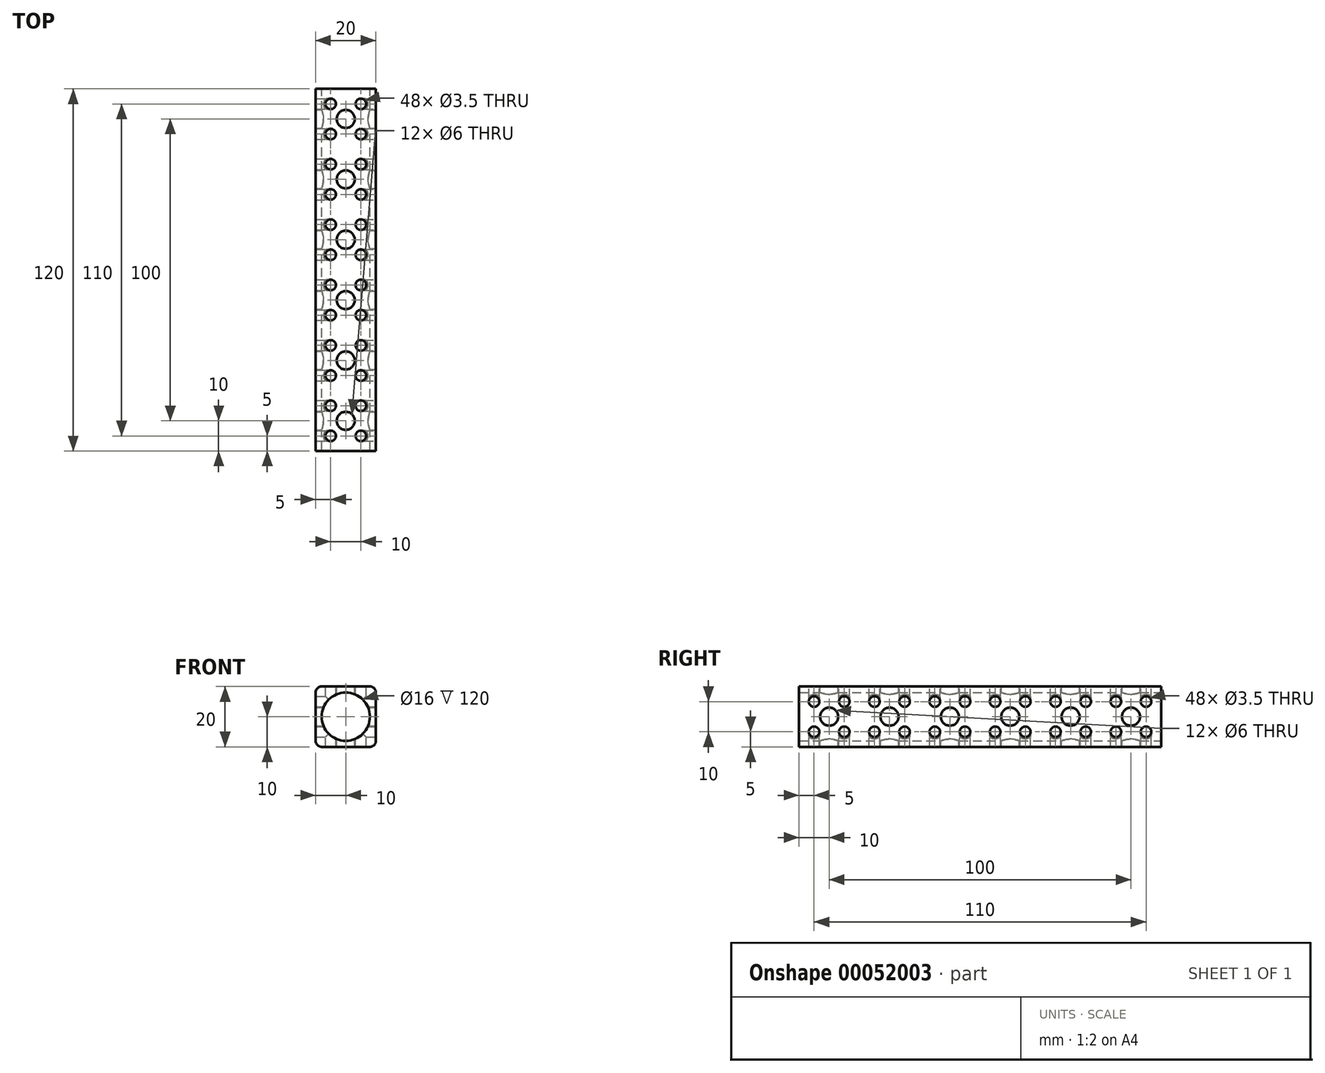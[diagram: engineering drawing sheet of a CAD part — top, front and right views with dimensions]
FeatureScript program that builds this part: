
annotation { "Feature Type Name" : "Feature", "Feature Type Description" : "" }
export const myFeature = defineFeature(function(context is Context, id is Id, definition is map)
    precondition{}
    {
        {
            var Q0;
            Q0=qCreatedBy(makeId("Front.planeOp"),FACE);
            var sketch = newSketch(context, id + "F0", { "sketchPlane" : qUnion([Q0])});
            skLineSegment(sketch, "E0.bottom", {"start": v(-10, 10) * mm, "end": v(10, 10) * mm});
            skLineSegment(sketch, "E0.top", {"start": v(-10, -10) * mm, "end": v(10, -10) * mm});
            skLineSegment(sketch, "E0.left", {"start": v(-10, 10) * mm, "end": v(-10, -10) * mm});
            skLineSegment(sketch, "E0.right", {"start": v(10, 10) * mm, "end": v(10, -10) * mm});
            skCircle(sketch, "E1", {"center": v(0, 0) * mm, "radius": 8 * mm});
            skLineSegment(sketch, "E2", {"start": v(-10, 10) * mm, "end": v(10, -10) * mm, "construction": true});
            skSolve(sketch);
        }
        {
            var Q0;
            Q0=makeQuery(id+"F0.imprint","IMPRINT",FACE,{"disambiguationData":[TD([[makeQuery(id+"F0.imprint","IMPRINT",EDGE,{"derivedFrom":sQuery(id+"F0.wireOp",EDGE,"E0.bottom")}),-1.0]])]});
            extrude(context, id + "F1", {"entities" : qUnion([Q0]), "endBound" : BoundingType.SYMMETRIC, "depth" : 120 * mm});
        }
        {
            var Q0;
            Q0=makeQuery(id+"F1.opExtrude","SWEPT_FACE",FACE,{"disambiguationData":[OSD([sQuery(id+"F0.wireOp",EDGE,"E0.right")])]});
            var sketch = newSketch(context, id + "F2", { "sketchPlane" : qUnion([Q0])});
            skLineSegment(sketch, "E3.bottom", {"start": v(-5, 5) * mm, "end": v(5, 5) * mm});
            skLineSegment(sketch, "E3.top", {"start": v(-5, -5) * mm, "end": v(5, -5) * mm});
            skLineSegment(sketch, "E3.left", {"start": v(-5, 5) * mm, "end": v(-5, -5) * mm});
            skLineSegment(sketch, "E3.right", {"start": v(5, 5) * mm, "end": v(5, -5) * mm});
            skLineSegment(sketch, "E4", {"start": v(-5, 5) * mm, "end": v(5, -5) * mm, "construction": true});
            skPoint(sketch, "E5", {"position": v(0, 0) * mm});
            skLineSegment(sketch, "E6.1.0.0", {"start": v(15, 5) * mm, "end": v(15, -5) * mm});
            skLineSegment(sketch, "E6.2.0.0", {"start": v(25, 5) * mm, "end": v(25, -5) * mm});
            skLineSegment(sketch, "E6.direction1", {"start": v(5, -5) * mm, "end": v(15, -5) * mm, "construction": true});
            skLineSegment(sketch, "E7.0.3.0", {"start": v(35, 5) * mm, "end": v(35, -5) * mm});
            skLineSegment(sketch, "E7.0.4.0", {"start": v(45, 5) * mm, "end": v(45, -5) * mm});
            skLineSegment(sketch, "E7.0.5.0", {"start": v(55, 5) * mm, "end": v(55, -5) * mm});
            skLineSegment(sketch, "E8.1.0.0", {"start": v(-15, 5) * mm, "end": v(-15, -5) * mm});
            skLineSegment(sketch, "E8.2.0.0", {"start": v(-25, 5) * mm, "end": v(-25, -5) * mm});
            skLineSegment(sketch, "E8.3.0.0", {"start": v(-35, 5) * mm, "end": v(-35, -5) * mm});
            skLineSegment(sketch, "E8.4.0.0", {"start": v(-45, 5) * mm, "end": v(-45, -5) * mm});
            skLineSegment(sketch, "E8.5.0.0", {"start": v(-55, 5) * mm, "end": v(-55, -5) * mm});
            skLineSegment(sketch, "E8.direction1", {"start": v(-5, -5) * mm, "end": v(-15, -5) * mm, "construction": true});
            skSolve(sketch);
        }
        {
            var Q0;
            Q0=sQuery(id+"F2.wireOp",VERTEX,"E8.5.0.0.start");
            var Q1;
            Q1=sQuery(id+"F2.wireOp",VERTEX,"E8.5.0.0.end");
            var Q2;
            Q2=sQuery(id+"F2.wireOp",VERTEX,"E8.4.0.0.end");
            var Q3;
            Q3=sQuery(id+"F2.wireOp",VERTEX,"E8.4.0.0.start");
            var Q4;
            Q4=sQuery(id+"F2.wireOp",VERTEX,"E8.3.0.0.start");
            var Q5;
            Q5=sQuery(id+"F2.wireOp",VERTEX,"E8.3.0.0.end");
            var Q6;
            Q6=sQuery(id+"F2.wireOp",VERTEX,"E8.2.0.0.end");
            var Q7;
            Q7=sQuery(id+"F2.wireOp",VERTEX,"E8.2.0.0.start");
            var Q8;
            Q8=sQuery(id+"F2.wireOp",VERTEX,"E8.direction1.end");
            var Q9;
            Q9=sQuery(id+"F2.wireOp",VERTEX,"E8.1.0.0.start");
            var Q10;
            Q10=sQuery(id+"F2.wireOp",VERTEX,"E3.left.end");
            var Q11;
            Q11=sQuery(id+"F2.wireOp",VERTEX,"E3.left.start");
            var Q12;
            Q12=sQuery(id+"F2.wireOp",VERTEX,"E3.top.end");
            var Q13;
            Q13=sQuery(id+"F2.wireOp",VERTEX,"E3.right.start");
            var Q14;
            Q14=sQuery(id+"F2.wireOp",VERTEX,"E6.direction1.end");
            var Q15;
            Q15=sQuery(id+"F2.wireOp",VERTEX,"E6.1.0.0.start");
            var Q16;
            Q16=sQuery(id+"F2.wireOp",VERTEX,"E6.2.0.0.end");
            var Q17;
            Q17=sQuery(id+"F2.wireOp",VERTEX,"E6.2.0.0.start");
            var Q18;
            Q18=sQuery(id+"F2.wireOp",VERTEX,"E7.0.3.0.start");
            var Q19;
            Q19=sQuery(id+"F2.wireOp",VERTEX,"E7.0.3.0.end");
            var Q20;
            Q20=sQuery(id+"F2.wireOp",VERTEX,"E7.0.4.0.end");
            var Q21;
            Q21=sQuery(id+"F2.wireOp",VERTEX,"E7.0.4.0.start");
            var Q22;
            Q22=sQuery(id+"F2.wireOp",VERTEX,"E7.0.5.0.end");
            var Q23;
            Q23=sQuery(id+"F2.wireOp",VERTEX,"E7.0.5.0.start");
            var Q24;
            Q24=makeQuery(id+"F1.opExtrude","SWEPT_BODY",BODY,{"disambiguationData":[OSD([sQuery(id+"F0.wireOp",EDGE,"E0.bottom"),sQuery(id+"F0.wireOp",EDGE,"E0.top"),sQuery(id+"F0.wireOp",EDGE,"E0.left"),sQuery(id+"F0.wireOp",EDGE,"E0.right"),sQuery(id+"F0.wireOp",EDGE,"E1")])]});
            hole(context, id + "F3", {"style" : HoleStyle.SIMPLE, "endStyle" : HoleEndStyle.THROUGH, "holeDiameter" : 3.5 * mm, "tappedDepth" : 12 * mm, "tapClearance" : 3, "locations" : qUnion([Q0, Q1, Q2, Q3, Q4, Q5, Q6, Q7, Q8, Q9, Q10, Q11, Q12, Q13, Q14, Q15, Q16, Q17, Q18, Q19, Q20, Q21, Q22, Q23]), "scope" : qUnion([Q24])});
        }
        {
            var Q0;
            Q0=makeQuery(id+"F1.opExtrude","SWEPT_FACE",FACE,{"disambiguationData":[OSD([sQuery(id+"F0.wireOp",EDGE,"E0.bottom")])]});
            var sketch = newSketch(context, id + "F4", { "sketchPlane" : qUnion([Q0])});
            skLineSegment(sketch, "E9.bottom", {"start": v(-5, 5) * mm, "end": v(5, 5) * mm});
            skLineSegment(sketch, "E9.top", {"start": v(-5, -5) * mm, "end": v(5, -5) * mm});
            skLineSegment(sketch, "E9.left", {"start": v(-5, 5) * mm, "end": v(-5, -5) * mm});
            skLineSegment(sketch, "E9.right", {"start": v(5, 5) * mm, "end": v(5, -5) * mm});
            skLineSegment(sketch, "E10", {"start": v(-5, 5) * mm, "end": v(5, -5) * mm, "construction": true});
            skPoint(sketch, "E11", {"position": v(0, 0) * mm});
            skLineSegment(sketch, "E12.0.1.0", {"start": v(-5, 15) * mm, "end": v(5, 15) * mm});
            skLineSegment(sketch, "E12.0.2.0", {"start": v(-5, 25) * mm, "end": v(5, 25) * mm});
            skLineSegment(sketch, "E12.0.3.0", {"start": v(-5, 35) * mm, "end": v(5, 35) * mm});
            skLineSegment(sketch, "E12.0.4.0", {"start": v(-5, 45) * mm, "end": v(5, 45) * mm});
            skLineSegment(sketch, "E12.0.5.0", {"start": v(-5, 55) * mm, "end": v(5, 55) * mm});
            skLineSegment(sketch, "E12.direction1", {"start": v(-5, 5) * mm, "end": v(20, 5) * mm, "construction": true});
            skLineSegment(sketch, "E12.direction2", {"start": v(-5, 5) * mm, "end": v(-5, 15) * mm, "construction": true});
            skLineSegment(sketch, "E13.0.1.0", {"start": v(-5, -15) * mm, "end": v(5, -15) * mm});
            skLineSegment(sketch, "E13.0.2.0", {"start": v(-5, -25) * mm, "end": v(5, -25) * mm});
            skLineSegment(sketch, "E13.0.3.0", {"start": v(-5, -35) * mm, "end": v(5, -35) * mm});
            skLineSegment(sketch, "E13.0.4.0", {"start": v(-5, -45) * mm, "end": v(5, -45) * mm});
            skLineSegment(sketch, "E13.0.5.0", {"start": v(-5, -55) * mm, "end": v(5, -55) * mm});
            skLineSegment(sketch, "E13.direction1", {"start": v(-5, -5) * mm, "end": v(5, -5) * mm, "construction": true});
            skLineSegment(sketch, "E13.direction2", {"start": v(-5, -5) * mm, "end": v(-5, -15) * mm, "construction": true});
            skSolve(sketch);
        }
        {
            var Q0;
            Q0=sQuery(id+"F4.wireOp",VERTEX,"E12.0.5.0.start");
            var Q1;
            Q1=sQuery(id+"F4.wireOp",VERTEX,"E12.0.5.0.end");
            var Q2;
            Q2=sQuery(id+"F4.wireOp",VERTEX,"E12.0.4.0.end");
            var Q3;
            Q3=sQuery(id+"F4.wireOp",VERTEX,"E12.0.4.0.start");
            var Q4;
            Q4=sQuery(id+"F4.wireOp",VERTEX,"E12.0.3.0.start");
            var Q5;
            Q5=sQuery(id+"F4.wireOp",VERTEX,"E12.0.3.0.end");
            var Q6;
            Q6=sQuery(id+"F4.wireOp",VERTEX,"E12.0.2.0.end");
            var Q7;
            Q7=sQuery(id+"F4.wireOp",VERTEX,"E12.0.2.0.start");
            var Q8;
            Q8=sQuery(id+"F4.wireOp",VERTEX,"E12.direction2.end");
            var Q9;
            Q9=sQuery(id+"F4.wireOp",VERTEX,"E12.0.1.0.end");
            var Q10;
            Q10=sQuery(id+"F4.wireOp",VERTEX,"E9.bottom.end");
            var Q11;
            Q11=sQuery(id+"F4.wireOp",VERTEX,"E12.direction1.start");
            var Q12;
            Q12=sQuery(id+"F4.wireOp",VERTEX,"E13.direction1.start");
            var Q13;
            Q13=sQuery(id+"F4.wireOp",VERTEX,"E9.top.end");
            var Q14;
            Q14=sQuery(id+"F4.wireOp",VERTEX,"E13.0.1.0.end");
            var Q15;
            Q15=sQuery(id+"F4.wireOp",VERTEX,"E13.direction2.end");
            var Q16;
            Q16=sQuery(id+"F4.wireOp",VERTEX,"E13.0.2.0.start");
            var Q17;
            Q17=sQuery(id+"F4.wireOp",VERTEX,"E13.0.2.0.end");
            var Q18;
            Q18=sQuery(id+"F4.wireOp",VERTEX,"E13.0.3.0.end");
            var Q19;
            Q19=sQuery(id+"F4.wireOp",VERTEX,"E13.0.3.0.start");
            var Q20;
            Q20=sQuery(id+"F4.wireOp",VERTEX,"E13.0.4.0.start");
            var Q21;
            Q21=sQuery(id+"F4.wireOp",VERTEX,"E13.0.4.0.end");
            var Q22;
            Q22=sQuery(id+"F4.wireOp",VERTEX,"E13.0.5.0.end");
            var Q23;
            Q23=sQuery(id+"F4.wireOp",VERTEX,"E13.0.5.0.start");
            var Q24;
            Q24=makeQuery(id+"F1.opExtrude","SWEPT_BODY",BODY,{"disambiguationData":[OSD([sQuery(id+"F0.wireOp",EDGE,"E0.bottom"),sQuery(id+"F0.wireOp",EDGE,"E0.top"),sQuery(id+"F0.wireOp",EDGE,"E0.left"),sQuery(id+"F0.wireOp",EDGE,"E0.right"),sQuery(id+"F0.wireOp",EDGE,"E1")])]});
            hole(context, id + "F5", {"style" : HoleStyle.SIMPLE, "endStyle" : HoleEndStyle.THROUGH, "holeDiameter" : 3.5 * mm, "tappedDepth" : 12 * mm, "tapClearance" : 3, "locations" : qUnion([Q0, Q1, Q2, Q3, Q4, Q5, Q6, Q7, Q8, Q9, Q10, Q11, Q12, Q13, Q14, Q15, Q16, Q17, Q18, Q19, Q20, Q21, Q22, Q23]), "scope" : qUnion([Q24])});
        }
        {
            var Q0;
            Q0=makeQuery(id+"F1.opExtrude","SWEPT_FACE",FACE,{"disambiguationData":[OSD([sQuery(id+"F0.wireOp",EDGE,"E0.right")])]});
            var sketch = newSketch(context, id + "F6", { "sketchPlane" : qUnion([Q0])});
            skPoint(sketch, "E14", {"position": v(0, 0) * mm});
            skPoint(sketch, "E15.1.0.0", {"position": v(10, 0) * mm});
            skPoint(sketch, "E15.2.0.0", {"position": v(20, 0) * mm});
            skPoint(sketch, "E15.3.0.0", {"position": v(30, 0) * mm});
            skPoint(sketch, "E15.4.0.0", {"position": v(40, 0) * mm});
            skPoint(sketch, "E15.5.0.0", {"position": v(50, 0) * mm});
            skLineSegment(sketch, "E15.direction1", {"start": v(0, 0) * mm, "end": v(10, 0) * mm, "construction": true});
            skPoint(sketch, "E16.1.0.0", {"position": v(-10, 0) * mm});
            skPoint(sketch, "E16.2.0.0", {"position": v(-20, 0) * mm});
            skPoint(sketch, "E16.3.0.0", {"position": v(-30, 0) * mm});
            skPoint(sketch, "E16.4.0.0", {"position": v(-40, 0) * mm});
            skPoint(sketch, "E16.5.0.0", {"position": v(-50, 0) * mm});
            skLineSegment(sketch, "E16.direction1", {"start": v(0, 0) * mm, "end": v(-10, 0) * mm, "construction": true});
            skSolve(sketch);
        }
        {
            var Q0;
            Q0=sQuery(id+"F6.wireOp",VERTEX,"E16.5.0.0");
            var Q1;
            Q1=sQuery(id+"F6.wireOp",VERTEX,"E16.3.0.0");
            var Q2;
            Q2=sQuery(id+"F6.wireOp",VERTEX,"E15.1.0.0");
            var Q3;
            Q3=sQuery(id+"F6.wireOp",VERTEX,"E15.3.0.0");
            var Q4;
            Q4=sQuery(id+"F6.wireOp",VERTEX,"E15.5.0.0");
            var Q5;
            Q5=sQuery(id+"F6.wireOp",VERTEX,"E16.1.0.0");
            var Q6;
            Q6=makeQuery(id+"F1.opExtrude","SWEPT_BODY",BODY,{"disambiguationData":[OSD([sQuery(id+"F0.wireOp",EDGE,"E0.bottom"),sQuery(id+"F0.wireOp",EDGE,"E0.top"),sQuery(id+"F0.wireOp",EDGE,"E0.left"),sQuery(id+"F0.wireOp",EDGE,"E0.right"),sQuery(id+"F0.wireOp",EDGE,"E1")])]});
            hole(context, id + "F7", {"style" : HoleStyle.SIMPLE, "endStyle" : HoleEndStyle.THROUGH, "holeDiameter" : 6 * mm, "tappedDepth" : 12 * mm, "tapClearance" : 3, "locations" : qUnion([Q0, Q1, Q2, Q3, Q4, Q5]), "scope" : qUnion([Q6]), "majorDiameter" : 5 * mm});
        }
        {
            var Q0;
            Q0=makeQuery(id+"F1.opExtrude","SWEPT_FACE",FACE,{"disambiguationData":[OSD([sQuery(id+"F0.wireOp",EDGE,"E0.bottom")])]});
            var sketch = newSketch(context, id + "F8", { "sketchPlane" : qUnion([Q0])});
            skLineSegment(sketch, "E17", {"start": v(0, 0) * mm, "end": v(0, 10) * mm});
            skLineSegment(sketch, "E18", {"start": v(0, 0) * mm, "end": v(0, -10) * mm});
            skLineSegment(sketch, "E19", {"start": v(0, 10) * mm, "end": v(0, 20) * mm});
            skLineSegment(sketch, "E20", {"start": v(0, 20) * mm, "end": v(0, 30) * mm});
            skLineSegment(sketch, "E21", {"start": v(0, 30) * mm, "end": v(0, 40) * mm});
            skLineSegment(sketch, "E22", {"start": v(0, 40) * mm, "end": v(0, 50) * mm});
            skLineSegment(sketch, "E23", {"start": v(0, -10) * mm, "end": v(0, -20) * mm});
            skLineSegment(sketch, "E24", {"start": v(0, -20) * mm, "end": v(0, -30) * mm});
            skLineSegment(sketch, "E25", {"start": v(0, -30) * mm, "end": v(0, -40) * mm});
            skLineSegment(sketch, "E26", {"start": v(0, -40) * mm, "end": v(0, -50) * mm});
            skSolve(sketch);
        }
        {
            var Q0;
            Q0=sQuery(id+"F8.wireOp",VERTEX,"E26.end");
            var Q1;
            Q1=sQuery(id+"F8.wireOp",VERTEX,"E24.end");
            var Q2;
            Q2=sQuery(id+"F8.wireOp",VERTEX,"E23.start");
            var Q3;
            Q3=sQuery(id+"F8.wireOp",VERTEX,"E19.start");
            var Q4;
            Q4=sQuery(id+"F8.wireOp",VERTEX,"E21.start");
            var Q5;
            Q5=sQuery(id+"F8.wireOp",VERTEX,"E22.end");
            var Q6;
            Q6=makeQuery(id+"F1.opExtrude","SWEPT_BODY",BODY,{"disambiguationData":[OSD([sQuery(id+"F0.wireOp",EDGE,"E0.bottom"),sQuery(id+"F0.wireOp",EDGE,"E0.top"),sQuery(id+"F0.wireOp",EDGE,"E0.left"),sQuery(id+"F0.wireOp",EDGE,"E0.right"),sQuery(id+"F0.wireOp",EDGE,"E1")])]});
            hole(context, id + "F9", {"style" : HoleStyle.SIMPLE, "endStyle" : HoleEndStyle.THROUGH, "holeDiameter" : 6 * mm, "tappedDepth" : 12 * mm, "tapClearance" : 3, "locations" : qUnion([Q0, Q1, Q2, Q3, Q4, Q5]), "scope" : qUnion([Q6])});
        }
        {
            var Q0;
            Q0=makeQuery(id+"F1.opExtrude","SWEPT_EDGE",EDGE,{"disambiguationData":[OSD([sQuery(id+"F0.wireOp",EDGE,"E0.bottom"),sQuery(id+"F0.wireOp",EDGE,"E0.left")])]});
            var Q1;
            Q1=makeQuery(id+"F1.opExtrude","SWEPT_EDGE",EDGE,{"disambiguationData":[OSD([sQuery(id+"F0.wireOp",EDGE,"E0.bottom"),sQuery(id+"F0.wireOp",EDGE,"E0.right")])]});
            var Q2;
            Q2=makeQuery(id+"F1.opExtrude","SWEPT_EDGE",EDGE,{"disambiguationData":[OSD([sQuery(id+"F0.wireOp",EDGE,"E0.top"),sQuery(id+"F0.wireOp",EDGE,"E0.right")])]});
            var Q3;
            Q3=makeQuery(id+"F1.opExtrude","SWEPT_EDGE",EDGE,{"disambiguationData":[OSD([sQuery(id+"F0.wireOp",EDGE,"E0.top"),sQuery(id+"F0.wireOp",EDGE,"E0.left")])]});
            fillet(context, id + "F10", {"entities" : qUnion([Q0, Q1, Q2, Q3]), "radius" : 2 * mm, "tangentPropagation" : true, "allowEdgeOverflow" : false});
        }
    });
